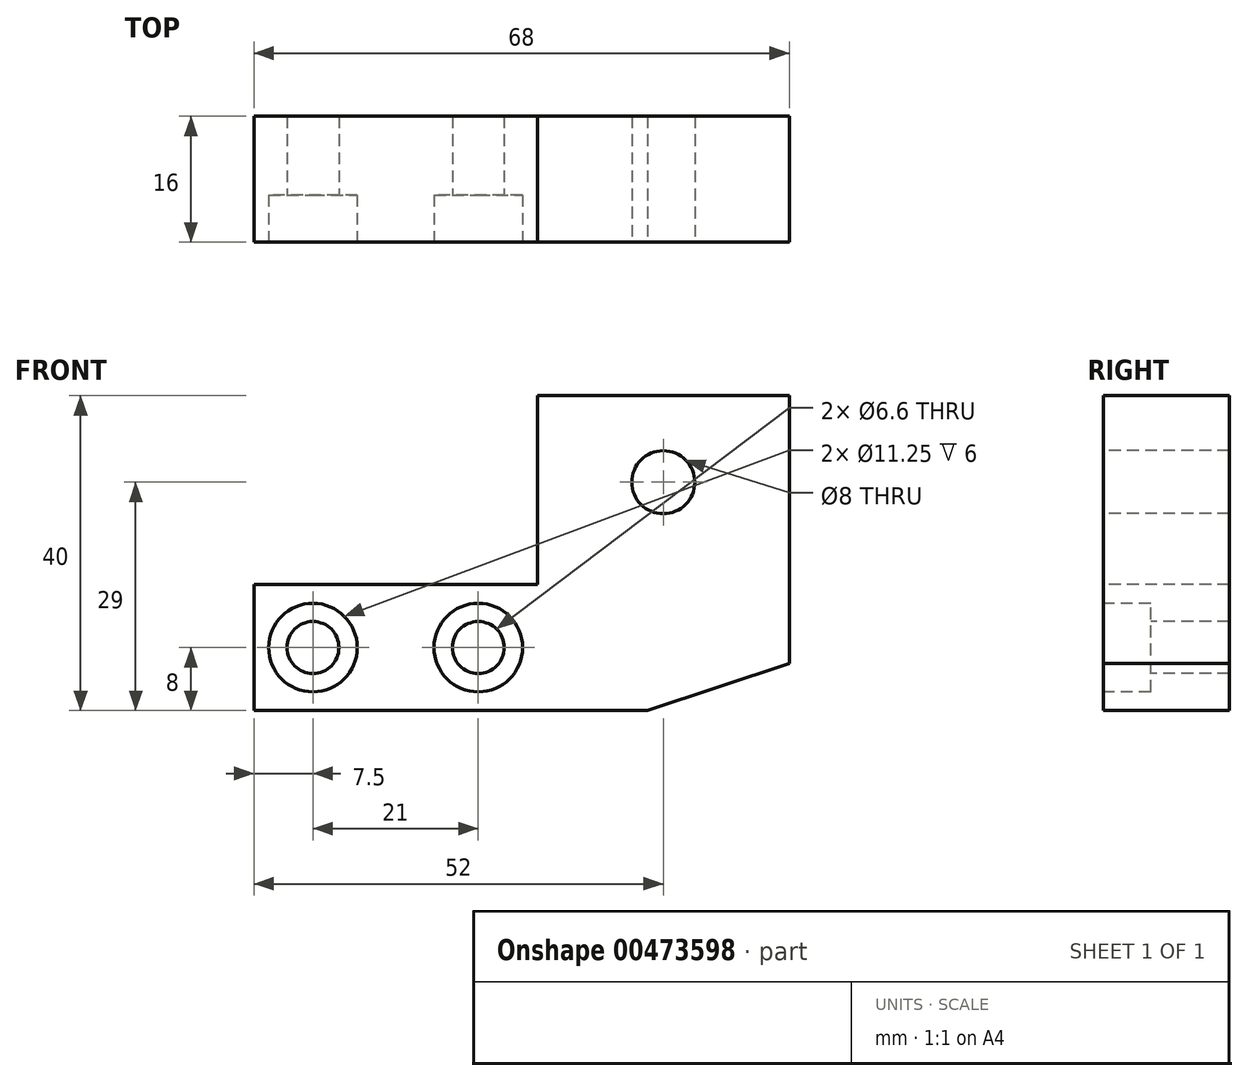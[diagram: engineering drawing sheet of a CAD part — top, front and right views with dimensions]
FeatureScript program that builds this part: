
annotation { "Feature Type Name" : "Feature", "Feature Type Description" : "" }
export const myFeature = defineFeature(function(context is Context, id is Id, definition is map)
    precondition{}
    {
        {
            var Q0;
            Q0=qCreatedBy(makeId("Front.planeOp"),FACE);
            var sketch = newSketch(context, id + "F0", { "sketchPlane" : qUnion([Q0])});
            skLineSegment(sketch, "E0.bottom", {"start": v(34, 20) * mm, "end": v(2, 20) * mm});
            skLineSegment(sketch, "E0.right", {"start": v(-34, -4) * mm, "end": v(-34, -20) * mm});
            skPoint(sketch, "E0.middle", {"position": v(0, 0) * mm});
            skLineSegment(sketch, "E1", {"start": v(16, -20) * mm, "end": v(-34, -20) * mm});
            skLineSegment(sketch, "E2", {"start": v(-34, -20) * mm, "end": v(-34, -4) * mm});
            skLineSegment(sketch, "E3", {"start": v(-34, -4) * mm, "end": v(2, -4) * mm});
            skPoint(sketch, "E4.end.orphan", {"position": v(2, 20) * mm});
            skLineSegment(sketch, "E5", {"start": v(2, -4) * mm, "end": v(2, 20) * mm});
            skLineSegment(sketch, "E6", {"start": v(18, -53.33) * mm, "end": v(18, 24.23) * mm, "construction": true});
            skCircle(sketch, "E7", {"center": v(18, 9) * mm, "radius": 4 * mm});
            skLineSegment(sketch, "E8", {"start": v(18, 24.23) * mm, "end": v(18, 60.34) * mm, "construction": true});
            skPoint(sketch, "E9.centerSnap0", {"position": v(-34, -12) * mm});
            skLineSegment(sketch, "E10", {"start": v(-26.5, -12) * mm, "end": v(-5.5, -12) * mm});
            skLineSegment(sketch, "E11", {"start": v(-16, 11.2) * mm, "end": v(-16, -54.56) * mm, "construction": true});
            skLineSegment(sketch, "E12", {"start": v(34, 20) * mm, "end": v(34, -14) * mm});
            skLineSegment(sketch, "E13", {"start": v(34, -14) * mm, "end": v(16, -20) * mm});
            skSolve(sketch);
        }
        {
            var Q0;
            Q0=makeQuery(id+"F0.imprint","IMPRINT",FACE,{"disambiguationData":[TD([[makeQuery(id+"F0.imprint","IMPRINT",EDGE,{"derivedFrom":sQuery(id+"F0.wireOp",EDGE,"E0.bottom")}),1.0]])]});
            extrude(context, id + "F1", {"entities" : qUnion([Q0]), "oppositeDirection" : true, "depth" : 16 * mm});
        }
        {
            var Q0;
            Q0=sQuery(id+"F0.wireOp",VERTEX,"E10.start");
            var Q1;
            Q1=sQuery(id+"F0.wireOp",VERTEX,"E10.end");
            var Q2;
            Q2=makeQuery(id+"F1.opExtrude","SWEPT_BODY",BODY,{"disambiguationData":[OSD([sQuery(id+"F0.wireOp",EDGE,"E0.bottom"),sQuery(id+"F0.wireOp",EDGE,"E1"),sQuery(id+"F0.wireOp",EDGE,"E2"),sQuery(id+"F0.wireOp",EDGE,"E3"),sQuery(id+"F0.wireOp",EDGE,"E5"),sQuery(id+"F0.wireOp",EDGE,"E7"),sQuery(id+"F0.wireOp",EDGE,"E12"),sQuery(id+"F0.wireOp",EDGE,"E13")])]});
            hole(context, id + "F2", {"style" : HoleStyle.C_BORE, "endStyle" : HoleEndStyle.THROUGH, "standardTappedOrClearance" : lookupTablePath({ "standard" : "ISO", "fit" : "Normal", "size" : "M6", "type" : "Clearance" }), "standardBlindInLast" : lookupTablePath({ "fit" : "Standard", "standard" : "ISO", "size" : "M6", "type" : "Clearance" }), "holeDiameter" : 6.6 * mm, "cBoreDiameter" : 11.25 * mm, "cBoreDepth" : 6 * mm, "isTappedThrough" : true, "tappedDepth" : 12 * mm, "tapClearance" : 3, "startFromSketch" : true, "locations" : qUnion([Q0, Q1]), "scope" : qUnion([Q2])});
        }
    });
